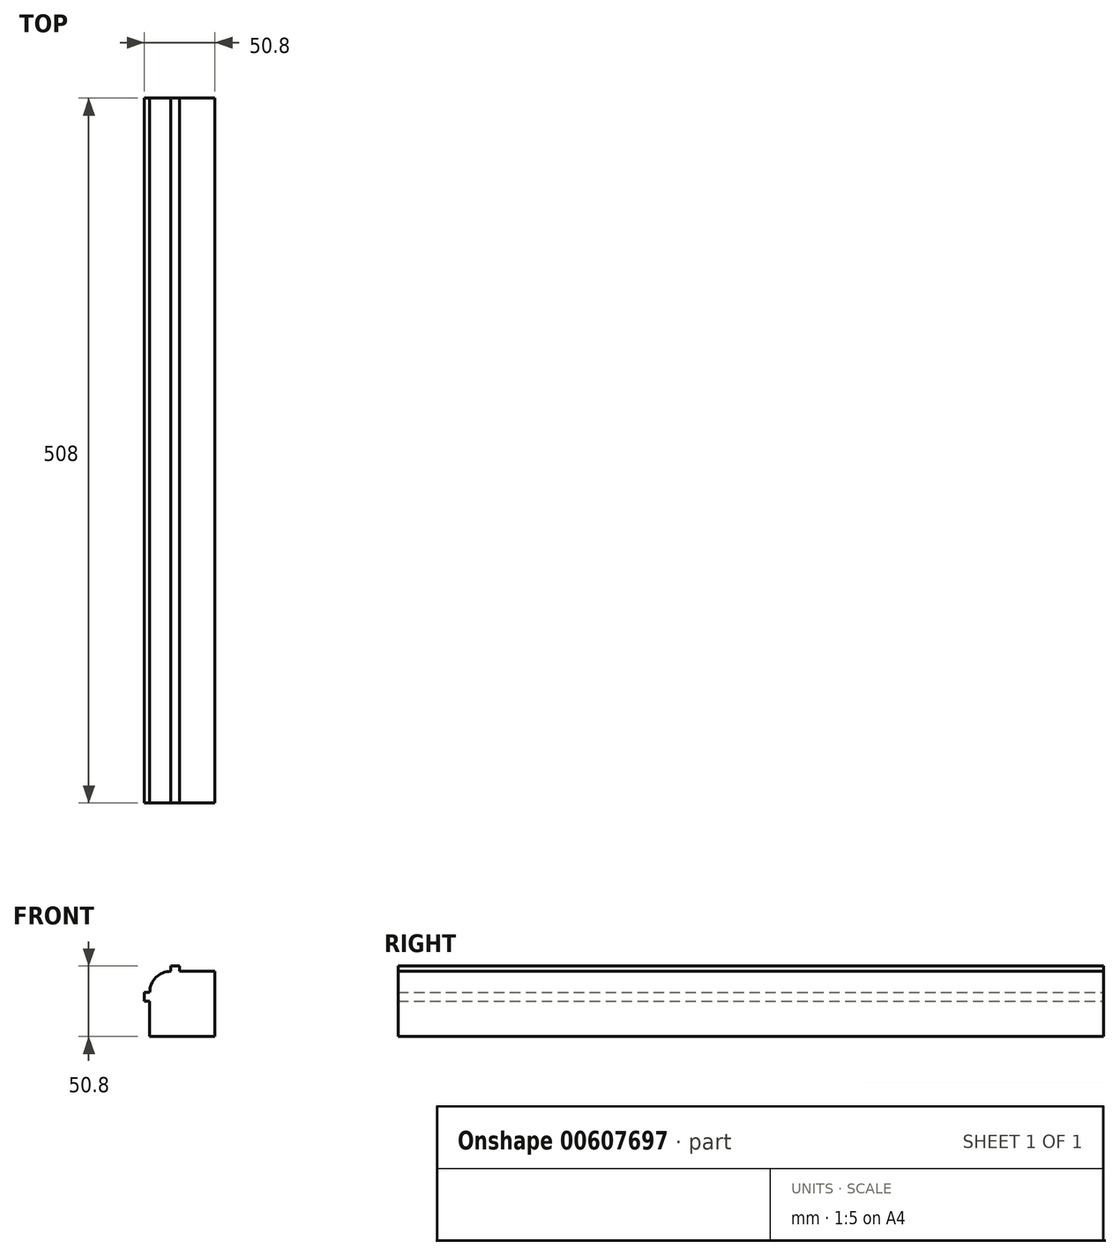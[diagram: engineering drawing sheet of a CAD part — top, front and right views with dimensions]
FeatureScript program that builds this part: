
annotation { "Feature Type Name" : "Feature", "Feature Type Description" : "" }
export const myFeature = defineFeature(function(context is Context, id is Id, definition is map)
    precondition{}
    {
        {
            var Q0;
            Q0=qCreatedBy(makeId("Top.planeOp"),FACE);
            var sketch = newSketch(context, id + "F0", { "sketchPlane" : qUnion([Q0])});
            skLineSegment(sketch, "E0.bottom", {"start": v(0, 0) * mm, "end": v(50.8, 0) * mm});
            skLineSegment(sketch, "E0.top", {"start": v(0, 508) * mm, "end": v(50.8, 508) * mm});
            skLineSegment(sketch, "E0.left", {"start": v(0, 0) * mm, "end": v(0, 508) * mm});
            skLineSegment(sketch, "E0.right", {"start": v(50.8, 0) * mm, "end": v(50.8, 508) * mm});
            skSolve(sketch);
        }
        {
            var Q0;
            Q0=makeQuery(id+"F0.imprint","IMPRINT",FACE,{"disambiguationData":[TD([[makeQuery(id+"F0.imprint","IMPRINT",EDGE,{"derivedFrom":sQuery(id+"F0.wireOp",EDGE,"E0.bottom")}),1.0]])]});
            extrude(context, id + "F1", {"entities" : qUnion([Q0]), "depth" : 50.8 * mm, "offsetDistance" : 25.4 * mm});
        }
        {
            var Q0;
            Q0=makeQuery(id+"F1.opExtrude","SWEPT_FACE",FACE,{"disambiguationData":[OSD([sQuery(id+"F0.wireOp",EDGE,"E0.top")])]});
            var sketch = newSketch(context, id + "F2", { "sketchPlane" : qUnion([Q0])});
            skLineSegment(sketch, "E1.bottom", {"start": v(-50.8, 50.8) * mm, "end": v(-25.4, 50.8) * mm});
            skLineSegment(sketch, "E1.top", {"start": v(-50.8, 47) * mm, "end": v(-25.4, 47) * mm});
            skLineSegment(sketch, "E1.left", {"start": v(-50.8, 50.8) * mm, "end": v(-50.8, 47) * mm});
            skLineSegment(sketch, "E1.right", {"start": v(-25.4, 50.8) * mm, "end": v(-25.4, 47) * mm});
            skSolve(sketch);
        }
        {
            var Q0;
            Q0=makeQuery(id+"F2.imprint","IMPRINT",FACE,{"disambiguationData":[TD([[makeQuery(id+"F2.imprint","IMPRINT",EDGE,{"derivedFrom":sQuery(id+"F2.wireOp",EDGE,"E1.bottom")}),1.0]])]});
            extrude(context, id + "F3", {"entities" : qUnion([Q0]), "operationType" : NewBodyOperationType.REMOVE, "endBound" : BoundingType.THROUGH_ALL, "oppositeDirection" : true, "depth" : 25.4 * mm, "offsetDistance" : 25.4 * mm});
        }
        {
            var Q0;
            Q0=makeQuery(id+"F1.opExtrude","SWEPT_FACE",FACE,{"disambiguationData":[OSD([sQuery(id+"F0.wireOp",EDGE,"E0.top")])]});
            var sketch = newSketch(context, id + "F4", { "sketchPlane" : qUnion([Q0])});
            skLineSegment(sketch, "E2.bottom", {"start": v(0, 0) * mm, "end": v(-3.81, 0) * mm});
            skLineSegment(sketch, "E2.top", {"start": v(0, 25.4) * mm, "end": v(-3.81, 25.4) * mm});
            skLineSegment(sketch, "E2.left", {"start": v(0, 0) * mm, "end": v(0, 25.4) * mm});
            skLineSegment(sketch, "E2.right", {"start": v(-3.81, 0) * mm, "end": v(-3.81, 25.4) * mm});
            skSolve(sketch);
        }
        {
            var Q0;
            Q0=makeQuery(id+"F4.imprint","IMPRINT",FACE,{"disambiguationData":[TD([[makeQuery(id+"F4.imprint","IMPRINT",EDGE,{"derivedFrom":sQuery(id+"F4.wireOp",EDGE,"E2.bottom")}),-1.0]])]});
            extrude(context, id + "F5", {"entities" : qUnion([Q0]), "operationType" : NewBodyOperationType.REMOVE, "endBound" : BoundingType.THROUGH_ALL, "oppositeDirection" : true, "depth" : 25.4 * mm, "offsetDistance" : 25.4 * mm});
        }
        {
            var Q0;
            Q0=makeQuery(id+"F1.opExtrude","SWEPT_FACE",FACE,{"disambiguationData":[OSD([sQuery(id+"F0.wireOp",EDGE,"E0.top")])]});
            var sketch = newSketch(context, id + "F6", { "sketchPlane" : qUnion([Q0])});
            skLineSegment(sketch, "E3", {"start": v(-19.05, 50.8) * mm, "end": v(-19.05, 47) * mm});
            skLineSegment(sketch, "E4", {"start": v(0, 31.75) * mm, "end": v(-3.81, 31.75) * mm});
            skArc(sketch, "E5", {"start": v(-3.81, 31.75) * mm, "mid": v(-8.27, 42.53) * mm, "end": v(-19.05, 47) * mm});
            skLineSegment(sketch, "E6", {"start": v(-19.05, 50.8) * mm, "end": v(0, 50.8) * mm});
            skLineSegment(sketch, "E7", {"start": v(0, 50.8) * mm, "end": v(0, 31.75) * mm});
            skSolve(sketch);
        }
        {
            var Q0;
            Q0=makeQuery(id+"F6.imprint","IMPRINT",FACE,{"disambiguationData":[TD([[makeQuery(id+"F6.imprint","IMPRINT",EDGE,{"derivedFrom":sQuery(id+"F6.wireOp",EDGE,"E3")}),1.0]])]});
            extrude(context, id + "F7", {"entities" : qUnion([Q0]), "operationType" : NewBodyOperationType.REMOVE, "endBound" : BoundingType.THROUGH_ALL, "oppositeDirection" : true, "depth" : 25.4 * mm, "offsetDistance" : 25.4 * mm});
        }
    });
